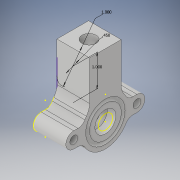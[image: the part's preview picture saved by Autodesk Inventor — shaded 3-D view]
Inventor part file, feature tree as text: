
AUTODESK INVENTOR PART (.ipt)
format: ipt  version: 2018 (Build 220112000, 112)  size: 274,944 bytes
history: native  units: in
note: dims shown in document units (in); Inventor stores cm internally (conversion verified against a paired STEP export)
features: sketch x8, other x5, extrude x4, projected_geometry x4, loft x3, revolve x2, fillet x2, pattern_circular x1
ambient origin geometry x8: Origin, YZ Plane, XZ Plane, XY Plane, X Axis, Y Axis, Z Axis, Center Point
bodies: Body1 (feature_tree)
feature tree (29):
  sketch  "Sketch2"  dims[d10=0.75in d11=0.65in]
  revolve  "Revolution1"  [1 undecoded]
  extrude  "Extrusion2"  Depth=0.25in
  fillet  "Fillet1"  Radius=1.0in
  pattern_circular  "Circular Pattern1"  Count=2 Angle=360.0deg
  revolve  "Revolution2"  [1 undecoded]
  extrude  "Extrusion8"  Depth=0.3325in
  sketch  "Sketch11"  dims[d23=1.0in d24=0.0in]
  extrude  "Extrusion9"  Depth=0.5in
  sketch  "Sketch14"  dims[d35=45.0deg d36=0.02in]
  loft  "Loft1"
  loft  "Loft2"
  loft  "Loft3"
  extrude  "Extrusion11"  Depth=0.5in
  fillet  "Fillet4"  Radius=1.0in
  sketch  "Sketch3"  dims[d13=90.0deg d20=0.25in d21=1.0in]
  sketch  "Sketch10"  dims[d22=0.5in]
  projected_geometry  "Projected Loop6"
  sketch  "Sketch12"  dims[d25=0.25in d26=0.7874in d27=360.0deg]
  projected_geometry  "Projected Loop7"
  sketch  "Sketch15"  dims[d38=0.225in d39=0.3325in]
  projected_geometry  "Projected Loop8"
  other  "Edges1"
  other  "Edges2"
  other  "Edges3"
  other  "Edges4"
  other  "Edges5"
  sketch  "Sketch16"  dims[d40=0.12in d41=0.5625in d42=90.0deg d60=0.275in d61=1.0in d62=0.45in d63=1.0in d64=0.5in d65=0.0in d67=0.125in d68=0.2in d69=0.2in d70=0.0in d71=0.75in d72=0.0in d75=0.45in d76=0.0in d77=90.0deg d78=0.0in d79=90.0deg d80=0.0in d81=90.0deg d82=0.0in d83=90.0deg d84=0.0in d85=90.0deg d86=0.0in d87=90.0deg d88=0.5in d89=0.0in d90=0.5in]
  projected_geometry  "Projected Loop9"
note: 2 required parameter values undecoded (feature->parameter linkage not recoverable at this tier; creation-order binding heuristic only, values carry confidence <= 0.55)
